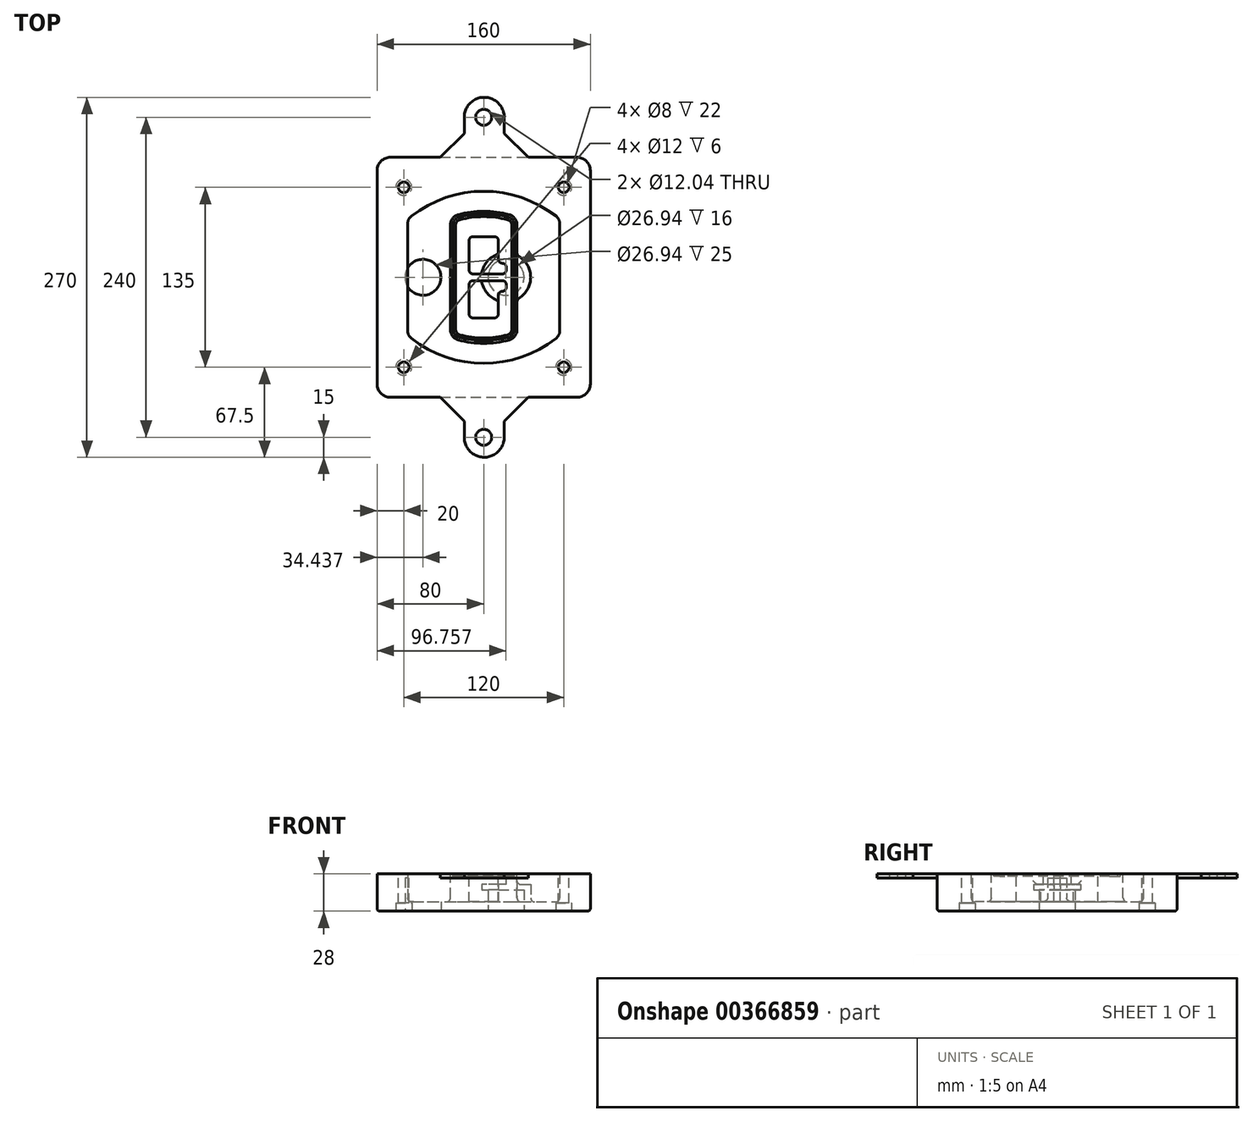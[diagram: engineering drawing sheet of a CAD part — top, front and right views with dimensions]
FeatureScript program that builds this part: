
annotation { "Feature Type Name" : "Feature", "Feature Type Description" : "" }
export const myFeature = defineFeature(function(context is Context, id is Id, definition is map)
    precondition{}
    {
        {
            var Q0;
            Q0=qCreatedBy(makeId("Top.planeOp"),FACE);
            var sketch = newSketch(context, id + "F0", { "sketchPlane" : qUnion([Q0])});
            skPoint(sketch, "E0.rect.middle", {"position": v(0, 0) * mm});
            skLineSegment(sketch, "E1.bottom", {"start": v(-70, -90) * mm, "end": v(70, -90) * mm});
            skLineSegment(sketch, "E1.top", {"start": v(-70, 90) * mm, "end": v(70, 90) * mm});
            skLineSegment(sketch, "E1.left", {"start": v(-80, -80) * mm, "end": v(-80, 80) * mm});
            skLineSegment(sketch, "E1.right", {"start": v(80, -80) * mm, "end": v(80, 80) * mm});
            skLineSegment(sketch, "E2", {"start": v(-80, 90) * mm, "end": v(80, -90) * mm, "construction": true});
            skLineSegment(sketch, "E3", {"start": v(80, 90) * mm, "end": v(-80, -90) * mm, "construction": true});
            skCircle(sketch, "E4", {"center": v(-60, 67.5) * mm, "radius": 4 * mm});
            skCircle(sketch, "E5", {"center": v(60, 67.5) * mm, "radius": 4 * mm});
            skCircle(sketch, "E6", {"center": v(60, -67.5) * mm, "radius": 4 * mm});
            skCircle(sketch, "E7", {"center": v(-60, -67.5) * mm, "radius": 4 * mm});
            skLineSegment(sketch, "E8", {"start": v(-60, 67.5) * mm, "end": v(60, 67.5) * mm, "construction": true});
            skLineSegment(sketch, "E9", {"start": v(60, 67.5) * mm, "end": v(60, -67.5) * mm, "construction": true});
            skLineSegment(sketch, "E10", {"start": v(60, -67.5) * mm, "end": v(-60, -67.5) * mm, "construction": true});
            skLineSegment(sketch, "E11", {"start": v(-60, -67.5) * mm, "end": v(-60, 67.5) * mm, "construction": true});
            skLineSegment(sketch, "E12", {"start": v(-60, 40.3) * mm, "end": v(-60, -40.3) * mm});
            skLineSegment(sketch, "E13", {"start": v(60, 40.3) * mm, "end": v(60, -40.3) * mm});
            skArc(sketch, "E14", {"start": v(56.15, 48.18) * mm, "mid": v(0, 67.5) * mm, "end": v(-56.15, 48.18) * mm});
            skArc(sketch, "E15", {"start": v(-56.15, -48.18) * mm, "mid": v(0, -67.5) * mm, "end": v(56.15, -48.18) * mm});
            skLineSegment(sketch, "E16", {"start": v(-60, 0) * mm, "end": v(60, 0) * mm, "construction": true});
            skPoint(sketch, "E17.visualSharp", {"position": v(-60, -45) * mm});
            skArc(sketch, "E17.filletArc", {"start": v(-60, -40.3) * mm, "mid": v(-58.99, -44.68) * mm, "end": v(-56.15, -48.18) * mm});
            skPoint(sketch, "E18.visualSharp", {"position": v(-60, 45) * mm});
            skArc(sketch, "E18.filletArc", {"start": v(-56.15, 48.18) * mm, "mid": v(-58.99, 44.68) * mm, "end": v(-60, 40.3) * mm});
            skPoint(sketch, "E19.visualSharp", {"position": v(60, 45) * mm});
            skArc(sketch, "E19.filletArc", {"start": v(60, 40.3) * mm, "mid": v(58.99, 44.68) * mm, "end": v(56.15, 48.18) * mm});
            skPoint(sketch, "E20.visualSharp", {"position": v(60, -45) * mm});
            skArc(sketch, "E20.filletArc", {"start": v(56.15, -48.18) * mm, "mid": v(58.99, -44.68) * mm, "end": v(60, -40.3) * mm});
            skPoint(sketch, "E21.visualSharp", {"position": v(-80, 90) * mm});
            skArc(sketch, "E21.filletArc", {"start": v(-70, 90) * mm, "mid": v(-77.07, 87.07) * mm, "end": v(-80, 80) * mm});
            skPoint(sketch, "E22.visualSharp", {"position": v(80, 90) * mm});
            skArc(sketch, "E22.filletArc", {"start": v(80, 80) * mm, "mid": v(77.07, 87.07) * mm, "end": v(70, 90) * mm});
            skPoint(sketch, "E23.visualSharp", {"position": v(80, -90) * mm});
            skArc(sketch, "E23.filletArc", {"start": v(70, -90) * mm, "mid": v(77.07, -87.07) * mm, "end": v(80, -80) * mm});
            skPoint(sketch, "E24.visualSharp", {"position": v(-80, -90) * mm});
            skArc(sketch, "E24.filletArc", {"start": v(-80, -80) * mm, "mid": v(-77.07, -87.07) * mm, "end": v(-70, -90) * mm});
            skArc(sketch, "E25.0", {"start": v(57, 40.3) * mm, "mid": v(56.3, 43.36) * mm, "end": v(54.3, 45.81) * mm});
            skLineSegment(sketch, "E25.1", {"start": v(57, 40.3) * mm, "end": v(57, -40.3) * mm});
            skArc(sketch, "E25.2", {"start": v(54.3, -45.81) * mm, "mid": v(56.3, -43.36) * mm, "end": v(57, -40.3) * mm});
            skArc(sketch, "E25.3", {"start": v(-54.3, -45.81) * mm, "mid": v(0, -64.5) * mm, "end": v(54.3, -45.81) * mm});
            skArc(sketch, "E25.4", {"start": v(-57, -40.3) * mm, "mid": v(-56.3, -43.36) * mm, "end": v(-54.3, -45.81) * mm});
            skArc(sketch, "E25.5", {"start": v(54.3, 45.81) * mm, "mid": v(0, 64.5) * mm, "end": v(-54.3, 45.81) * mm});
            skLineSegment(sketch, "E25.6", {"start": v(-57, 40.3) * mm, "end": v(-57, -40.3) * mm});
            skArc(sketch, "E25.7", {"start": v(-54.3, 45.81) * mm, "mid": v(-56.3, 43.36) * mm, "end": v(-57, 40.3) * mm});
            skArc(sketch, "E26.0", {"start": v(-58.62, 51.33) * mm, "mid": v(-62.58, 46.43) * mm, "end": v(-64, 40.3) * mm});
            skArc(sketch, "E26.1", {"start": v(58.62, 51.33) * mm, "mid": v(0, 71.5) * mm, "end": v(-58.62, 51.33) * mm});
            skArc(sketch, "E26.2", {"start": v(64, 40.3) * mm, "mid": v(62.58, 46.43) * mm, "end": v(58.62, 51.33) * mm});
            skLineSegment(sketch, "E26.3", {"start": v(64, 40.3) * mm, "end": v(64, -40.3) * mm});
            skArc(sketch, "E26.4", {"start": v(58.62, -51.33) * mm, "mid": v(62.58, -46.43) * mm, "end": v(64, -40.3) * mm});
            skLineSegment(sketch, "E26.5", {"start": v(-64, 40.3) * mm, "end": v(-64, -40.3) * mm});
            skArc(sketch, "E26.6", {"start": v(-58.62, -51.33) * mm, "mid": v(0, -71.5) * mm, "end": v(58.62, -51.33) * mm});
            skArc(sketch, "E26.7", {"start": v(-64, -40.3) * mm, "mid": v(-62.58, -46.43) * mm, "end": v(-58.62, -51.33) * mm});
            skSolve(sketch);
        }
        {
            var Q0;
            Q0=makeQuery(id+"F0.imprint","IMPRINT",FACE,{"disambiguationData":[TD([[makeQuery(id+"F0.imprint","IMPRINT",EDGE,{"derivedFrom":sQuery(id+"F0.wireOp",EDGE,"E1.bottom")}),1.0]])]});
            var Q1;
            Q1=makeQuery(id+"F0.imprint","IMPRINT",FACE,{"disambiguationData":[TD([[makeQuery(id+"F0.imprint","IMPRINT",EDGE,{"derivedFrom":sQuery(id+"F0.wireOp",EDGE,"E12")}),1.0]])]});
            var Q2;
            Q2=makeQuery(id+"F0.imprint","IMPRINT",FACE,{"disambiguationData":[TD([[makeQuery(id+"F0.imprint","IMPRINT",EDGE,{"derivedFrom":sQuery(id+"F0.wireOp",EDGE,"E25.0")}),1.0]])]});
            var Q3;
            Q3=makeQuery(id+"F0.imprint","IMPRINT",FACE,{"disambiguationData":[TD([[makeQuery(id+"F0.imprint","IMPRINT",EDGE,{"derivedFrom":sQuery(id+"F0.wireOp",EDGE,"E12")}),-1.0]])]});
            extrude(context, id + "F1", {"entities" : qUnion([Q0, Q1, Q2, Q3]), "oppositeDirection" : true, "depth" : 25 * mm});
        }
        {
            var Q0;
            Q0=makeQuery(id+"F0.imprint","IMPRINT",FACE,{"disambiguationData":[TD([[makeQuery(id+"F0.imprint","IMPRINT",EDGE,{"derivedFrom":sQuery(id+"F0.wireOp",EDGE,"E12")}),1.0]])]});
            extrude(context, id + "F2", {"entities" : qUnion([Q0]), "operationType" : NewBodyOperationType.ADD, "depth" : 3 * mm});
        }
        {
            var Q0;
            Q0=makeQuery(id+"F0.imprint","IMPRINT",FACE,{"disambiguationData":[TD([[makeQuery(id+"F0.imprint","IMPRINT",EDGE,{"derivedFrom":sQuery(id+"F0.wireOp",EDGE,"E25.0")}),1.0]])]});
            extrude(context, id + "F3", {"entities" : qUnion([Q0]), "operationType" : NewBodyOperationType.REMOVE, "oppositeDirection" : true, "depth" : 18 * mm});
        }
        {
            var Q0;
            Q0=makeQuery(id+"F2.opExtrude","CAP_FACE",FACE,{"disambiguationData":[OSD([sQuery(id+"F0.wireOp",EDGE,"E12"),sQuery(id+"F0.wireOp",EDGE,"E13"),sQuery(id+"F0.wireOp",EDGE,"E14"),sQuery(id+"F0.wireOp",EDGE,"E15"),sQuery(id+"F0.wireOp",EDGE,"E17.filletArc"),sQuery(id+"F0.wireOp",EDGE,"E18.filletArc"),sQuery(id+"F0.wireOp",EDGE,"E19.filletArc"),sQuery(id+"F0.wireOp",EDGE,"E20.filletArc"),sQuery(id+"F0.wireOp",EDGE,"E25.0"),sQuery(id+"F0.wireOp",EDGE,"E25.1"),sQuery(id+"F0.wireOp",EDGE,"E25.2"),sQuery(id+"F0.wireOp",EDGE,"E25.3"),sQuery(id+"F0.wireOp",EDGE,"E25.4"),sQuery(id+"F0.wireOp",EDGE,"E25.5"),sQuery(id+"F0.wireOp",EDGE,"E25.6"),sQuery(id+"F0.wireOp",EDGE,"E25.7")])],"isStart":false});
            var sketch = newSketch(context, id + "F4", { "sketchPlane" : qUnion([Q0])});
            skArc(sketch, "E27.0", {"start": v(-19.08, -46.97) * mm, "mid": v(0, -49.5) * mm, "end": v(19.08, -46.97) * mm});
            skArc(sketch, "E28.0", {"start": v(19.08, 46.97) * mm, "mid": v(0, 49.5) * mm, "end": v(-19.08, 46.97) * mm});
            skLineSegment(sketch, "E29", {"start": v(-25, 39.25) * mm, "end": v(-25, -39.25) * mm});
            skLineSegment(sketch, "E30", {"start": v(25, 39.25) * mm, "end": v(25, -39.25) * mm});
            skLineSegment(sketch, "E31", {"start": v(-25, 45.1) * mm, "end": v(25, 45.1) * mm, "construction": true});
            skLineSegment(sketch, "E32", {"start": v(-25, -45.1) * mm, "end": v(25, -45.1) * mm, "construction": true});
            skPoint(sketch, "E33.visualSharp", {"position": v(-25, 45.1) * mm});
            skArc(sketch, "E33.filletArc", {"start": v(-19.08, 46.97) * mm, "mid": v(-23.35, 44.11) * mm, "end": v(-25, 39.25) * mm});
            skPoint(sketch, "E34.visualSharp", {"position": v(25, 45.1) * mm});
            skArc(sketch, "E34.filletArc", {"start": v(25, 39.25) * mm, "mid": v(23.35, 44.11) * mm, "end": v(19.08, 46.97) * mm});
            skPoint(sketch, "E35.visualSharp", {"position": v(25, -45.1) * mm});
            skArc(sketch, "E35.filletArc", {"start": v(19.08, -46.97) * mm, "mid": v(23.35, -44.11) * mm, "end": v(25, -39.25) * mm});
            skPoint(sketch, "E36.visualSharp", {"position": v(-25, -45.1) * mm});
            skArc(sketch, "E36.filletArc", {"start": v(-25, -39.25) * mm, "mid": v(-23.35, -44.11) * mm, "end": v(-19.08, -46.97) * mm});
            skArc(sketch, "E37.0", {"start": v(54.3, 45.81) * mm, "mid": v(0, 64.5) * mm, "end": v(-54.3, 45.81) * mm});
            skArc(sketch, "E37.1", {"start": v(-54.3, 45.81) * mm, "mid": v(-56.3, 43.36) * mm, "end": v(-57, 40.3) * mm});
            skLineSegment(sketch, "E37.2", {"start": v(-57, 40.3) * mm, "end": v(-57, -40.3) * mm});
            skArc(sketch, "E37.3", {"start": v(-57, -40.3) * mm, "mid": v(-56.3, -43.36) * mm, "end": v(-54.3, -45.81) * mm});
            skArc(sketch, "E37.4", {"start": v(-54.3, -45.81) * mm, "mid": v(0, -64.5) * mm, "end": v(54.3, -45.81) * mm});
            skArc(sketch, "E37.5", {"start": v(54.3, -45.81) * mm, "mid": v(56.3, -43.36) * mm, "end": v(57, -40.3) * mm});
            skLineSegment(sketch, "E37.6", {"start": v(57, 40.3) * mm, "end": v(57, -40.3) * mm});
            skArc(sketch, "E37.7", {"start": v(57, 40.3) * mm, "mid": v(56.3, 43.36) * mm, "end": v(54.3, 45.81) * mm});
            skLineSegment(sketch, "E38.0", {"start": v(23, 39.25) * mm, "end": v(23, -39.25) * mm});
            skArc(sketch, "E38.1", {"start": v(18.56, -45.04) * mm, "mid": v(21.76, -42.9) * mm, "end": v(23, -39.25) * mm});
            skArc(sketch, "E38.2", {"start": v(-18.56, -45.04) * mm, "mid": v(0, -47.5) * mm, "end": v(18.56, -45.04) * mm});
            skArc(sketch, "E38.3", {"start": v(-23, -39.25) * mm, "mid": v(-21.76, -42.9) * mm, "end": v(-18.56, -45.04) * mm});
            skLineSegment(sketch, "E38.4", {"start": v(-23, 39.25) * mm, "end": v(-23, -39.25) * mm});
            skArc(sketch, "E38.5", {"start": v(23, 39.25) * mm, "mid": v(21.76, 42.9) * mm, "end": v(18.56, 45.04) * mm});
            skArc(sketch, "E38.6", {"start": v(-18.56, 45.04) * mm, "mid": v(-21.76, 42.9) * mm, "end": v(-23, 39.25) * mm});
            skArc(sketch, "E38.7", {"start": v(18.56, 45.04) * mm, "mid": v(0, 47.5) * mm, "end": v(-18.56, 45.04) * mm});
            skArc(sketch, "E39.0", {"start": v(21, 39.25) * mm, "mid": v(20.18, 41.68) * mm, "end": v(18.04, 43.1) * mm});
            skLineSegment(sketch, "E39.1", {"start": v(21, 39.25) * mm, "end": v(21, -39.25) * mm});
            skArc(sketch, "E39.2", {"start": v(18.04, -43.1) * mm, "mid": v(20.18, -41.68) * mm, "end": v(21, -39.25) * mm});
            skArc(sketch, "E39.3", {"start": v(-18.04, -43.1) * mm, "mid": v(0, -45.5) * mm, "end": v(18.04, -43.1) * mm});
            skArc(sketch, "E39.4", {"start": v(-21, -39.25) * mm, "mid": v(-20.18, -41.68) * mm, "end": v(-18.04, -43.1) * mm});
            skArc(sketch, "E39.5", {"start": v(18.04, 43.1) * mm, "mid": v(0, 45.5) * mm, "end": v(-18.04, 43.1) * mm});
            skLineSegment(sketch, "E39.6", {"start": v(-21, 39.25) * mm, "end": v(-21, -39.25) * mm});
            skArc(sketch, "E39.7", {"start": v(-18.04, 43.1) * mm, "mid": v(-20.18, 41.68) * mm, "end": v(-21, 39.25) * mm});
            skLineSegment(sketch, "E40", {"start": v(-25, 0) * mm, "end": v(25, 0) * mm, "construction": true});
            skLineSegment(sketch, "E41", {"start": v(-11, 5.5) * mm, "end": v(-11, 27.5) * mm});
            skLineSegment(sketch, "E42", {"start": v(-8, 30.5) * mm, "end": v(8, 30.5) * mm});
            skLineSegment(sketch, "E43", {"start": v(11, 27.5) * mm, "end": v(11, 13.5) * mm});
            skLineSegment(sketch, "E44", {"start": v(14, 10.5) * mm, "end": v(14, 10.5) * mm});
            skLineSegment(sketch, "E45", {"start": v(17, 7.5) * mm, "end": v(17, 5.5) * mm});
            skLineSegment(sketch, "E46", {"start": v(14, 2.5) * mm, "end": v(-8, 2.5) * mm});
            skPoint(sketch, "E47.visualSharp", {"position": v(-11, 30.5) * mm});
            skArc(sketch, "E47.filletArc", {"start": v(-8, 30.5) * mm, "mid": v(-10.12, 29.62) * mm, "end": v(-11, 27.5) * mm});
            skPoint(sketch, "E48.visualSharp", {"position": v(11, 30.5) * mm});
            skArc(sketch, "E48.filletArc", {"start": v(11, 27.5) * mm, "mid": v(10.12, 29.62) * mm, "end": v(8, 30.5) * mm});
            skPoint(sketch, "E49.visualSharp", {"position": v(11, 10.5) * mm});
            skArc(sketch, "E49.filletArc", {"start": v(11, 13.5) * mm, "mid": v(11.88, 11.38) * mm, "end": v(14, 10.5) * mm});
            skPoint(sketch, "E50.visualSharp", {"position": v(17, 10.5) * mm});
            skArc(sketch, "E50.filletArc", {"start": v(17, 7.5) * mm, "mid": v(16.12, 9.62) * mm, "end": v(14, 10.5) * mm});
            skPoint(sketch, "E51.visualSharp", {"position": v(17, 2.5) * mm});
            skArc(sketch, "E51.filletArc", {"start": v(14, 2.5) * mm, "mid": v(16.12, 3.38) * mm, "end": v(17, 5.5) * mm});
            skPoint(sketch, "E52.visualSharp", {"position": v(-11, 2.5) * mm});
            skArc(sketch, "E52.filletArc", {"start": v(-11, 5.5) * mm, "mid": v(-10.12, 3.38) * mm, "end": v(-8, 2.5) * mm});
            skLineSegment(sketch, "E53.0.MirrorCS", {"start": v(14, -2.5) * mm, "end": v(-8, -2.5) * mm});
            skArc(sketch, "E54.0.MirrorCS", {"start": v(-11, -5.5) * mm, "mid": v(-10.12, -3.38) * mm, "end": v(-8, -2.5) * mm});
            skLineSegment(sketch, "E55.0.MirrorCS", {"start": v(-11, -5.5) * mm, "end": v(-11, -27.5) * mm});
            skArc(sketch, "E56.0.MirrorCS", {"start": v(-8, -30.5) * mm, "mid": v(-10.12, -29.62) * mm, "end": v(-11, -27.5) * mm});
            skLineSegment(sketch, "E57.0.MirrorCS", {"start": v(-8, -30.5) * mm, "end": v(8, -30.5) * mm});
            skArc(sketch, "E58.0.MirrorCS", {"start": v(11, -27.5) * mm, "mid": v(10.12, -29.62) * mm, "end": v(8, -30.5) * mm});
            skLineSegment(sketch, "E59.0.MirrorCS", {"start": v(11, -27.5) * mm, "end": v(11, -13.5) * mm});
            skArc(sketch, "E60.0.MirrorCS", {"start": v(11, -13.5) * mm, "mid": v(11.88, -11.38) * mm, "end": v(14, -10.5) * mm});
            skArc(sketch, "E61.0.MirrorCS", {"start": v(17, -7.5) * mm, "mid": v(16.12, -9.62) * mm, "end": v(14, -10.5) * mm});
            skLineSegment(sketch, "E62.0.MirrorCS", {"start": v(17, -7.5) * mm, "end": v(17, -5.5) * mm});
            skArc(sketch, "E63.0.MirrorCS", {"start": v(14, -2.5) * mm, "mid": v(16.12, -3.38) * mm, "end": v(17, -5.5) * mm});
            skSolve(sketch);
        }
        {
            var Q0;
            Q0=makeQuery(id+"F4.imprint","IMPRINT",FACE,{"disambiguationData":[TD([[makeQuery(id+"F4.imprint","IMPRINT",EDGE,{"derivedFrom":sQuery(id+"F4.wireOp",EDGE,"E27.0")}),1.0]])]});
            var Q1;
            Q1=makeQuery(id+"F4.imprint","IMPRINT",FACE,{"disambiguationData":[TD([[makeQuery(id+"F4.imprint","IMPRINT",EDGE,{"derivedFrom":sQuery(id+"F4.wireOp",EDGE,"E38.0")}),-1.0]])]});
            var Q2;
            Q2=makeQuery(id+"F4.imprint","IMPRINT",FACE,{"disambiguationData":[TD([[makeQuery(id+"F4.imprint","IMPRINT",EDGE,{"derivedFrom":sQuery(id+"F4.wireOp",EDGE,"E39.0")}),1.0]])]});
            extrude(context, id + "F5", {"entities" : qUnion([Q0, Q1, Q2]), "operationType" : NewBodyOperationType.ADD, "endBound" : BoundingType.UP_TO_NEXT, "oppositeDirection" : true, "depth" : 25 * mm});
        }
        {
            var Q0;
            Q0=makeQuery(id+"F4.imprint","IMPRINT",FACE,{"disambiguationData":[TD([[makeQuery(id+"F4.imprint","IMPRINT",EDGE,{"derivedFrom":sQuery(id+"F4.wireOp",EDGE,"E38.0")}),-1.0]])]});
            extrude(context, id + "F6", {"entities" : qUnion([Q0]), "operationType" : NewBodyOperationType.REMOVE, "oppositeDirection" : true, "depth" : 2 * mm});
        }
        {
            var Q0;
            Q0=makeQuery(id+"F1.opExtrude","CAP_FACE",FACE,{"disambiguationData":[OSD([sQuery(id+"F0.wireOp",EDGE,"E1.bottom"),sQuery(id+"F0.wireOp",EDGE,"E1.top"),sQuery(id+"F0.wireOp",EDGE,"E1.left"),sQuery(id+"F0.wireOp",EDGE,"E1.right"),sQuery(id+"F0.wireOp",EDGE,"E4"),sQuery(id+"F0.wireOp",EDGE,"E5"),sQuery(id+"F0.wireOp",EDGE,"E6"),sQuery(id+"F0.wireOp",EDGE,"E7"),sQuery(id+"F0.wireOp",EDGE,"E21.filletArc"),sQuery(id+"F0.wireOp",EDGE,"E22.filletArc"),sQuery(id+"F0.wireOp",EDGE,"E23.filletArc"),sQuery(id+"F0.wireOp",EDGE,"E24.filletArc")])],"isStart":false});
            var sketch = newSketch(context, id + "F7", { "sketchPlane" : qUnion([Q0])});
            skCircle(sketch, "E64", {"center": v(16.76, 0) * mm, "radius": 13.47 * mm});
            skCircle(sketch, "E65", {"center": v(-45.56, 0) * mm, "radius": 13.47 * mm});
            skLineSegment(sketch, "E66", {"start": v(80, 0) * mm, "end": v(-80, 0) * mm});
            skCircle(sketch, "E67", {"center": v(16.76, 0) * mm, "radius": 18.47 * mm});
            skCircle(sketch, "E68", {"center": v(60, -67.5) * mm, "radius": 6 * mm});
            skCircle(sketch, "E69", {"center": v(-60, -67.5) * mm, "radius": 6 * mm});
            skCircle(sketch, "E70", {"center": v(-60, 67.5) * mm, "radius": 6 * mm});
            skCircle(sketch, "E71", {"center": v(60, 67.5) * mm, "radius": 6 * mm});
            skSolve(sketch);
        }
        {
            var Q0;
            {var subQ1=sQuery(id+"F7.wireOp",EDGE,"E66");var subQ4=sQuery(id+"F7.wireOp",EDGE,"E64");var subQ6=makeQuery(id+"F7.imprint","INTERSECT",VERTEX,{"disambiguationData":[OD(0.0)],"derivedFrom":[subQ4,subQ1]});Q0=makeQuery(id+"F7.imprint","IMPRINT",FACE,{"disambiguationData":[TD([[makeQuery(id+"F7.imprint","IMPRINT",EDGE,{"disambiguationData":[TD([[subQ6,-1.0]])],"derivedFrom":subQ4}),-1.0]])]});}
            var Q1;
            {var subQ0=sQuery(id+"F7.wireOp",EDGE,"E66");var subQ1=sQuery(id+"F7.wireOp",EDGE,"E64");var subQ3=makeQuery(id+"F7.imprint","INTERSECT",VERTEX,{"disambiguationData":[OD(0.0)],"derivedFrom":[subQ1,subQ0]});Q1=makeQuery(id+"F7.imprint","IMPRINT",FACE,{"disambiguationData":[TD([[makeQuery(id+"F7.imprint","IMPRINT",EDGE,{"disambiguationData":[TD([[subQ3,-1.0]])],"derivedFrom":subQ1}),1.0]])]});}
            var Q2;
            {var subQ0=sQuery(id+"F7.wireOp",EDGE,"E66");var subQ1=sQuery(id+"F7.wireOp",EDGE,"E64");var subQ3=makeQuery(id+"F7.imprint","INTERSECT",VERTEX,{"disambiguationData":[OD(0.0)],"derivedFrom":[subQ1,subQ0]});Q2=makeQuery(id+"F7.imprint","IMPRINT",FACE,{"disambiguationData":[TD([[makeQuery(id+"F7.imprint","IMPRINT",EDGE,{"disambiguationData":[TD([[subQ3,1.0]])],"derivedFrom":subQ1}),1.0]])]});}
            var Q3;
            {var subQ1=sQuery(id+"F7.wireOp",EDGE,"E66");var subQ4=sQuery(id+"F7.wireOp",EDGE,"E64");var subQ6=makeQuery(id+"F7.imprint","INTERSECT",VERTEX,{"disambiguationData":[OD(0.0)],"derivedFrom":[subQ4,subQ1]});Q3=makeQuery(id+"F7.imprint","IMPRINT",FACE,{"disambiguationData":[TD([[makeQuery(id+"F7.imprint","IMPRINT",EDGE,{"disambiguationData":[TD([[subQ6,1.0]])],"derivedFrom":subQ4}),-1.0]])]});}
            extrude(context, id + "F8", {"entities" : qUnion([Q0, Q1, Q2, Q3]), "operationType" : NewBodyOperationType.ADD, "oppositeDirection" : true, "depth" : 20 * mm});
        }
        {
            var Q0;
            {var subQ0=sQuery(id+"F7.wireOp",EDGE,"E66");var subQ1=sQuery(id+"F7.wireOp",EDGE,"E64");var subQ3=makeQuery(id+"F7.imprint","INTERSECT",VERTEX,{"disambiguationData":[OD(0.0)],"derivedFrom":[subQ1,subQ0]});Q0=makeQuery(id+"F7.imprint","IMPRINT",FACE,{"disambiguationData":[TD([[makeQuery(id+"F7.imprint","IMPRINT",EDGE,{"disambiguationData":[TD([[subQ3,-1.0]])],"derivedFrom":subQ1}),1.0]])]});}
            var Q1;
            {var subQ0=sQuery(id+"F7.wireOp",EDGE,"E66");var subQ1=sQuery(id+"F7.wireOp",EDGE,"E64");var subQ3=makeQuery(id+"F7.imprint","INTERSECT",VERTEX,{"disambiguationData":[OD(0.0)],"derivedFrom":[subQ1,subQ0]});Q1=makeQuery(id+"F7.imprint","IMPRINT",FACE,{"disambiguationData":[TD([[makeQuery(id+"F7.imprint","IMPRINT",EDGE,{"disambiguationData":[TD([[subQ3,1.0]])],"derivedFrom":subQ1}),1.0]])]});}
            extrude(context, id + "F9", {"entities" : qUnion([Q0, Q1]), "operationType" : NewBodyOperationType.REMOVE, "oppositeDirection" : true, "depth" : 16 * mm});
        }
        {
            var Q0;
            {var subQ0=sQuery(id+"F7.wireOp",EDGE,"E66");var subQ1=sQuery(id+"F7.wireOp",EDGE,"E65");var subQ3=makeQuery(id+"F7.imprint","INTERSECT",VERTEX,{"disambiguationData":[OD(0.0)],"derivedFrom":[subQ1,subQ0]});Q0=makeQuery(id+"F7.imprint","IMPRINT",FACE,{"disambiguationData":[TD([[makeQuery(id+"F7.imprint","IMPRINT",EDGE,{"disambiguationData":[TD([[subQ3,-1.0]])],"derivedFrom":subQ1}),1.0]])]});}
            var Q1;
            {var subQ0=sQuery(id+"F7.wireOp",EDGE,"E66");var subQ1=sQuery(id+"F7.wireOp",EDGE,"E65");var subQ3=makeQuery(id+"F7.imprint","INTERSECT",VERTEX,{"disambiguationData":[OD(0.0)],"derivedFrom":[subQ1,subQ0]});Q1=makeQuery(id+"F7.imprint","IMPRINT",FACE,{"disambiguationData":[TD([[makeQuery(id+"F7.imprint","IMPRINT",EDGE,{"disambiguationData":[TD([[subQ3,1.0]])],"derivedFrom":subQ1}),1.0]])]});}
            extrude(context, id + "F10", {"entities" : qUnion([Q0, Q1]), "operationType" : NewBodyOperationType.REMOVE, "oppositeDirection" : true, "depth" : 25 * mm});
        }
        {
            var Q0;
            Q0=makeQuery(id+"F7.imprint","IMPRINT",FACE,{"disambiguationData":[TD([[makeQuery(id+"F7.imprint","IMPRINT",EDGE,{"derivedFrom":sQuery(id+"F7.wireOp",EDGE,"E68")}),1.0]])]});
            var Q1;
            Q1=makeQuery(id+"F7.imprint","IMPRINT",FACE,{"disambiguationData":[TD([[makeQuery(id+"F7.imprint","IMPRINT",EDGE,{"derivedFrom":makeQuery(id+"F1.opExtrude","CAP_EDGE",EDGE,{"disambiguationData":[OSD([sQuery(id+"F0.wireOp",EDGE,"E5")])],"isStart":false})}),-1.0]])]});
            var Q2;
            Q2=makeQuery(id+"F7.imprint","IMPRINT",FACE,{"disambiguationData":[TD([[makeQuery(id+"F7.imprint","IMPRINT",EDGE,{"derivedFrom":sQuery(id+"F7.wireOp",EDGE,"E69")}),1.0]])]});
            var Q3;
            Q3=makeQuery(id+"F7.imprint","IMPRINT",FACE,{"disambiguationData":[TD([[makeQuery(id+"F7.imprint","IMPRINT",EDGE,{"derivedFrom":makeQuery(id+"F1.opExtrude","CAP_EDGE",EDGE,{"disambiguationData":[OSD([sQuery(id+"F0.wireOp",EDGE,"E4")])],"isStart":false})}),-1.0]])]});
            var Q4;
            Q4=makeQuery(id+"F7.imprint","IMPRINT",FACE,{"disambiguationData":[TD([[makeQuery(id+"F7.imprint","IMPRINT",EDGE,{"derivedFrom":sQuery(id+"F7.wireOp",EDGE,"E70")}),1.0]])]});
            var Q5;
            Q5=makeQuery(id+"F7.imprint","IMPRINT",FACE,{"disambiguationData":[TD([[makeQuery(id+"F7.imprint","IMPRINT",EDGE,{"derivedFrom":makeQuery(id+"F1.opExtrude","CAP_EDGE",EDGE,{"disambiguationData":[OSD([sQuery(id+"F0.wireOp",EDGE,"E7")])],"isStart":false})}),-1.0]])]});
            var Q6;
            Q6=makeQuery(id+"F7.imprint","IMPRINT",FACE,{"disambiguationData":[TD([[makeQuery(id+"F7.imprint","IMPRINT",EDGE,{"derivedFrom":sQuery(id+"F7.wireOp",EDGE,"E71")}),1.0]])]});
            var Q7;
            Q7=makeQuery(id+"F7.imprint","IMPRINT",FACE,{"disambiguationData":[TD([[makeQuery(id+"F7.imprint","IMPRINT",EDGE,{"derivedFrom":makeQuery(id+"F1.opExtrude","CAP_EDGE",EDGE,{"disambiguationData":[OSD([sQuery(id+"F0.wireOp",EDGE,"E6")])],"isStart":false})}),-1.0]])]});
            var Q8;
            Q8 = qSketchRegion(id + "F16", true);
            extrude(context, id + "F11", {"entities" : qUnion([Q0, Q1, Q2, Q3, Q4, Q5, Q6, Q7, Q8]), "operationType" : NewBodyOperationType.REMOVE, "oppositeDirection" : true, "depth" : 6 * mm});
        }
        {
            var Q0;
            Q0=makeQuery(id+"F9.boolean.opBoolean","COPY",FACE,{"derivedFrom":makeQuery(id+"F9.opExtrude","CAP_FACE",FACE,{"disambiguationData":[OSD([sQuery(id+"F7.wireOp",EDGE,"E64")])],"isStart":false})});
            var sketch = newSketch(context, id + "F12", { "sketchPlane" : qUnion([Q0])});
            skArc(sketch, "E72.0", {"start": v(11, 17.55) * mm, "mid": v(2.57, 11.82) * mm, "end": v(-1.54, 2.5) * mm});
            skArc(sketch, "E72.1", {"start": v(-1.54, -2.5) * mm, "mid": v(2.57, -11.82) * mm, "end": v(11, -17.55) * mm});
            skLineSegment(sketch, "E73", {"start": v(-1.54, -2.5) * mm, "end": v(14, -2.5) * mm});
            skLineSegment(sketch, "E74.0", {"start": v(14, 2.5) * mm, "end": v(-1.54, 2.5) * mm});
            skArc(sketch, "E74.1", {"start": v(14, 2.5) * mm, "mid": v(16.12, 3.38) * mm, "end": v(17, 5.5) * mm});
            skLineSegment(sketch, "E74.2", {"start": v(17, 7.5) * mm, "end": v(17, 5.5) * mm});
            skArc(sketch, "E74.3", {"start": v(17, 7.5) * mm, "mid": v(16.12, 9.62) * mm, "end": v(14, 10.5) * mm});
            skArc(sketch, "E74.4", {"start": v(11, 13.5) * mm, "mid": v(11.88, 11.38) * mm, "end": v(14, 10.5) * mm});
            skLineSegment(sketch, "E74.5", {"start": v(11, 17.55) * mm, "end": v(11, 13.5) * mm});
            skLineSegment(sketch, "E74.7", {"start": v(14, -2.5) * mm, "end": v(-1.54, -2.5) * mm});
            skArc(sketch, "E74.8", {"start": v(14, -2.5) * mm, "mid": v(16.12, -3.38) * mm, "end": v(17, -5.5) * mm});
            skLineSegment(sketch, "E74.9", {"start": v(17, -7.5) * mm, "end": v(17, -5.5) * mm});
            skArc(sketch, "E74.10", {"start": v(17, -7.5) * mm, "mid": v(16.12, -9.62) * mm, "end": v(14, -10.5) * mm});
            skArc(sketch, "E74.11", {"start": v(11, -13.5) * mm, "mid": v(11.88, -11.38) * mm, "end": v(14, -10.5) * mm});
            skLineSegment(sketch, "E74.12", {"start": v(11, -17.55) * mm, "end": v(11, -13.5) * mm});
            skPoint(sketch, "E75.orphan", {"position": v(11, -27.5) * mm});
            skPoint(sketch, "E76.orphan", {"position": v(-8, -2.5) * mm});
            skPoint(sketch, "E77.orphan", {"position": v(-8, 2.5) * mm});
            skPoint(sketch, "E78.orphan", {"position": v(11, 27.5) * mm});
            skSolve(sketch);
        }
        {
            var Q0;
            {var subQ7=sQuery(id+"F12.wireOp",EDGE,"E72.0");var subQ14=sQuery(id+"F12.wireOp",EDGE,"E72.1");var subQ16=sQuery(id+"F12.wireOp",EDGE,"E74.1");var subQ18=sQuery(id+"F12.wireOp",EDGE,"E74.8");Q0=qUnion([makeQuery(id+"F12.imprint","IMPRINT",FACE,{"disambiguationData":[TD([[makeQuery(id+"F12.imprint","IMPRINT",EDGE,{"derivedFrom":subQ7}),1.0]])]}),makeQuery(id+"F12.imprint","IMPRINT",FACE,{"disambiguationData":[TD([[makeQuery(id+"F12.imprint","IMPRINT",EDGE,{"derivedFrom":subQ14}),1.0]])]}),makeQuery(id+"F12.imprint","IMPRINT",FACE,{"disambiguationData":[TD([[makeQuery(id+"F12.imprint","IMPRINT",EDGE,{"derivedFrom":subQ16}),1.0]])]}),makeQuery(id+"F12.imprint","IMPRINT",FACE,{"disambiguationData":[TD([[makeQuery(id+"F12.imprint","IMPRINT",EDGE,{"derivedFrom":subQ18}),-1.0]])]})]);}
            var Q1;
            Q1=makeQuery(id+"F5.boolean.opBoolean","SPLIT",FACE,{"disambiguationData":[TD([makeQuery(id+"F5.opExtrude","SWEPT_FACE",FACE,{"disambiguationData":[OSD([sQuery(id+"F4.wireOp",EDGE,"E41")])]})])],"derivedFrom":makeQuery(id+"F3.boolean.opBoolean","COPY",FACE,{"derivedFrom":makeQuery(id+"F3.opExtrude","CAP_FACE",FACE,{"disambiguationData":[OSD([sQuery(id+"F0.wireOp",EDGE,"E25.0"),sQuery(id+"F0.wireOp",EDGE,"E25.1"),sQuery(id+"F0.wireOp",EDGE,"E25.2"),sQuery(id+"F0.wireOp",EDGE,"E25.3"),sQuery(id+"F0.wireOp",EDGE,"E25.4"),sQuery(id+"F0.wireOp",EDGE,"E25.5"),sQuery(id+"F0.wireOp",EDGE,"E25.6"),sQuery(id+"F0.wireOp",EDGE,"E25.7")])],"isStart":false})})});
            extrude(context, id + "F13", {"entities" : qUnion([Q0]), "operationType" : NewBodyOperationType.REMOVE, "endBound" : BoundingType.UP_TO_SURFACE, "endBoundEntityFace" : qUnion([Q1]), "depth" : 25 * mm});
        }
        {
            var Q0;
            Q0=makeQuery(id+"F1.opExtrude","CAP_EDGE",EDGE,{"disambiguationData":[OSD([sQuery(id+"F0.wireOp",EDGE,"E1.bottom")])],"isStart":false});
            fillet(context, id + "F14", {"entities" : qUnion([Q0]), "radius" : 2 * mm, "tangentPropagation" : true, "allowEdgeOverflow" : false});
        }
        {
            var Q0;
            Q0=makeQuery(id+"F3.boolean.opBoolean","COPY",EDGE,{"derivedFrom":makeQuery(id+"F3.opExtrude","CAP_EDGE",EDGE,{"disambiguationData":[OSD([sQuery(id+"F0.wireOp",EDGE,"E25.6")])],"isStart":false})});
            var Q1;
            Q1=makeQuery(id+"F8.boolean.opBoolean","INTERSECT",EDGE,{"derivedFrom":[makeQuery(id+"F5.opExtrude","SWEPT_FACE",FACE,{"disambiguationData":[OSD([sQuery(id+"F4.wireOp",EDGE,"E30")])]}),makeQuery(id+"F8.opExtrude","CAP_FACE",FACE,{"disambiguationData":[OSD([sQuery(id+"F7.wireOp",EDGE,"E67")])],"isStart":false})]});
            var Q2;
            Q2=makeQuery(id+"F8.boolean.opBoolean","INTERSECT",EDGE,{"disambiguationData":[OD(1.0)],"derivedFrom":[makeQuery(id+"F5.opExtrude","SWEPT_FACE",FACE,{"disambiguationData":[OSD([sQuery(id+"F4.wireOp",EDGE,"E30")])]}),makeQuery(id+"F8.opExtrude","SWEPT_FACE",FACE,{"disambiguationData":[OSD([sQuery(id+"F7.wireOp",EDGE,"E67")])]})]});
            var Q3;
            {var subQ0=sQuery(id+"F4.wireOp",EDGE,"E30");Q3=makeQuery(id+"F8.boolean.opBoolean","SPLIT",EDGE,{"disambiguationData":[TD([makeQuery(id+"F5.opExtrude","SWEPT_FACE",FACE,{"disambiguationData":[OSD([sQuery(id+"F4.wireOp",EDGE,"E35.filletArc")])]})])],"derivedFrom":makeQuery(id+"F5.opExtrude","CAP_EDGE",EDGE,{"disambiguationData":[OSD([subQ0])],"isStart":false})});}
            var Q4;
            {var subQ0=sQuery(id+"F0.wireOp",EDGE,"E25.7");var subQ1=sQuery(id+"F0.wireOp",EDGE,"E25.1");var subQ2=sQuery(id+"F0.wireOp",EDGE,"E25.6");var subQ3=sQuery(id+"F0.wireOp",EDGE,"E25.5");var subQ4=sQuery(id+"F0.wireOp",EDGE,"E25.4");var subQ5=sQuery(id+"F0.wireOp",EDGE,"E25.0");var subQ6=sQuery(id+"F0.wireOp",EDGE,"E25.2");var subQ7=sQuery(id+"F0.wireOp",EDGE,"E25.3");Q4=makeQuery(id+"F8.boolean.opBoolean","INTERSECT",EDGE,{"derivedFrom":[makeQuery(id+"F5.boolean.opBoolean","SPLIT",FACE,{"disambiguationData":[TD([makeQuery(id+"F2.opExtrude","SWEPT_FACE",FACE,{"disambiguationData":[OSD([subQ5])]})])],"derivedFrom":makeQuery(id+"F3.boolean.opBoolean","COPY",FACE,{"derivedFrom":makeQuery(id+"F3.opExtrude","CAP_FACE",FACE,{"disambiguationData":[OSD([subQ5,subQ1,subQ6,subQ7,subQ4,subQ3,subQ2,subQ0])],"isStart":false})})}),makeQuery(id+"F8.opExtrude","SWEPT_FACE",FACE,{"disambiguationData":[OSD([sQuery(id+"F7.wireOp",EDGE,"E67")])]})]});}
            var Q5;
            Q5=makeQuery(id+"F8.boolean.opBoolean","INTERSECT",EDGE,{"disambiguationData":[OD(0.0)],"derivedFrom":[makeQuery(id+"F5.opExtrude","SWEPT_FACE",FACE,{"disambiguationData":[OSD([sQuery(id+"F4.wireOp",EDGE,"E30")])]}),makeQuery(id+"F8.opExtrude","SWEPT_FACE",FACE,{"disambiguationData":[OSD([sQuery(id+"F7.wireOp",EDGE,"E67")])]})]});
            fillet(context, id + "F15", {"entities" : qUnion([Q0, Q1, Q2, Q3, Q4, Q5]), "radius" : 3 * mm, "tangentPropagation" : true, "allowEdgeOverflow" : false});
        }
        {
            var Q0;
            {var subQ0=sQuery(id+"F0.wireOp",EDGE,"E21.filletArc");var subQ1=sQuery(id+"F0.wireOp",EDGE,"E7");var subQ2=sQuery(id+"F0.wireOp",EDGE,"E6");var subQ3=sQuery(id+"F0.wireOp",EDGE,"E5");var subQ4=sQuery(id+"F0.wireOp",EDGE,"E4");var subQ5=sQuery(id+"F0.wireOp",EDGE,"E22.filletArc");var subQ6=sQuery(id+"F0.wireOp",EDGE,"E1.bottom");var subQ7=sQuery(id+"F0.wireOp",EDGE,"E1.right");var subQ8=sQuery(id+"F0.wireOp",EDGE,"E1.top");var subQ9=sQuery(id+"F0.wireOp",EDGE,"E1.left");var subQ10=sQuery(id+"F0.wireOp",EDGE,"E23.filletArc");var subQ11=sQuery(id+"F0.wireOp",EDGE,"E24.filletArc");Q0=makeQuery(id+"F2.boolean.opBoolean","SPLIT",FACE,{"disambiguationData":[TD([makeQuery(id+"F1.opExtrude","SWEPT_FACE",FACE,{"disambiguationData":[OSD([subQ6])]})])],"derivedFrom":makeQuery(id+"F1.opExtrude","CAP_FACE",FACE,{"disambiguationData":[OSD([subQ6,subQ8,subQ9,subQ7,subQ4,subQ3,subQ2,subQ1,subQ0,subQ5,subQ10,subQ11])],"isStart":true})});}
            var sketch = newSketch(context, id + "F16", { "sketchPlane" : qUnion([Q0])});
            skCircle(sketch, "E79", {"center": v(0, 120) * mm, "radius": 6.02 * mm});
            skLineSegment(sketch, "E80", {"start": v(-32.6, 90) * mm, "end": v(-14.6, 108) * mm});
            skLineSegment(sketch, "E81", {"start": v(-14.6, 108) * mm, "end": v(-14.6, 119.83) * mm});
            skLineSegment(sketch, "E82", {"start": v(15.39, 108) * mm, "end": v(15.39, 120) * mm});
            skArc(sketch, "E83", {"start": v(15.39, 120) * mm, "mid": v(0.3, 135) * mm, "end": v(-14.6, 119.83) * mm});
            skLineSegment(sketch, "E84", {"start": v(15.39, 108) * mm, "end": v(33.39, 90) * mm});
            skLineSegment(sketch, "E85", {"start": v(-100.74, 0) * mm, "end": v(97.7, 0) * mm, "construction": true});
            skPoint(sketch, "E85.endSnap0", {"position": v(60, 0) * mm});
            skLineSegment(sketch, "E86.MirrorCS", {"start": v(-14.6, -108) * mm, "end": v(-14.6, -119.83) * mm});
            skLineSegment(sketch, "E87.MirrorCS", {"start": v(-32.6, -90) * mm, "end": v(-14.6, -108) * mm});
            skCircle(sketch, "E88.MirrorC", {"center": v(0, -120) * mm, "radius": 6.02 * mm});
            skArc(sketch, "E89.MirrorCS", {"start": v(15.39, -120) * mm, "mid": v(0.3, -135) * mm, "end": v(-14.6, -119.83) * mm});
            skLineSegment(sketch, "E90.MirrorCS", {"start": v(15.39, -108) * mm, "end": v(15.39, -120) * mm});
            skLineSegment(sketch, "E91.MirrorCS", {"start": v(15.39, -108) * mm, "end": v(33.39, -90) * mm});
            skLineSegment(sketch, "E92", {"start": v(0.39, 120) * mm, "end": v(0.39, 90) * mm, "construction": true});
            skLineSegment(sketch, "E93", {"start": v(0.39, -120) * mm, "end": v(0.39, -90) * mm, "construction": true});
            skSolve(sketch);
        }
        {
            var Q0;
            Q0=makeQuery(id+"F16.imprint","IMPRINT",FACE,{"disambiguationData":[TD([[makeQuery(id+"F16.imprint","IMPRINT",EDGE,{"derivedFrom":makeQuery(id+"F1.opExtrude","CAP_EDGE",EDGE,{"disambiguationData":[OSD([sQuery(id+"F0.wireOp",EDGE,"E1.left")])],"isStart":true})}),-1.0]])]});
            var Q1;
            Q1=makeQuery(id+"F16.imprint","IMPRINT",FACE,{"disambiguationData":[TD([[makeQuery(id+"F16.imprint","IMPRINT",EDGE,{"derivedFrom":sQuery(id+"F16.wireOp",EDGE,"E79")}),-1.0]])]});
            var Q2;
            Q2=makeQuery(id+"F16.imprint","IMPRINT",FACE,{"disambiguationData":[TD([[makeQuery(id+"F16.imprint","IMPRINT",EDGE,{"derivedFrom":sQuery(id+"F16.wireOp",EDGE,"E86.MirrorCS")}),1.0]])]});
            var Q3;
            Q3=makeQuery(id+"F2.opExtrude","CAP_FACE",FACE,{"disambiguationData":[OSD([sQuery(id+"F0.wireOp",EDGE,"E12"),sQuery(id+"F0.wireOp",EDGE,"E13"),sQuery(id+"F0.wireOp",EDGE,"E14"),sQuery(id+"F0.wireOp",EDGE,"E15"),sQuery(id+"F0.wireOp",EDGE,"E17.filletArc"),sQuery(id+"F0.wireOp",EDGE,"E18.filletArc"),sQuery(id+"F0.wireOp",EDGE,"E19.filletArc"),sQuery(id+"F0.wireOp",EDGE,"E20.filletArc"),sQuery(id+"F0.wireOp",EDGE,"E25.0"),sQuery(id+"F0.wireOp",EDGE,"E25.1"),sQuery(id+"F0.wireOp",EDGE,"E25.2"),sQuery(id+"F0.wireOp",EDGE,"E25.3"),sQuery(id+"F0.wireOp",EDGE,"E25.4"),sQuery(id+"F0.wireOp",EDGE,"E25.5"),sQuery(id+"F0.wireOp",EDGE,"E25.6"),sQuery(id+"F0.wireOp",EDGE,"E25.7")])],"isStart":false});
            extrude(context, id + "F17", {"entities" : qUnion([Q0, Q1, Q2]), "operationType" : NewBodyOperationType.ADD, "endBound" : BoundingType.UP_TO_SURFACE, "endBoundEntityFace" : qUnion([Q3]), "depth" : 25 * mm});
        }
    });
